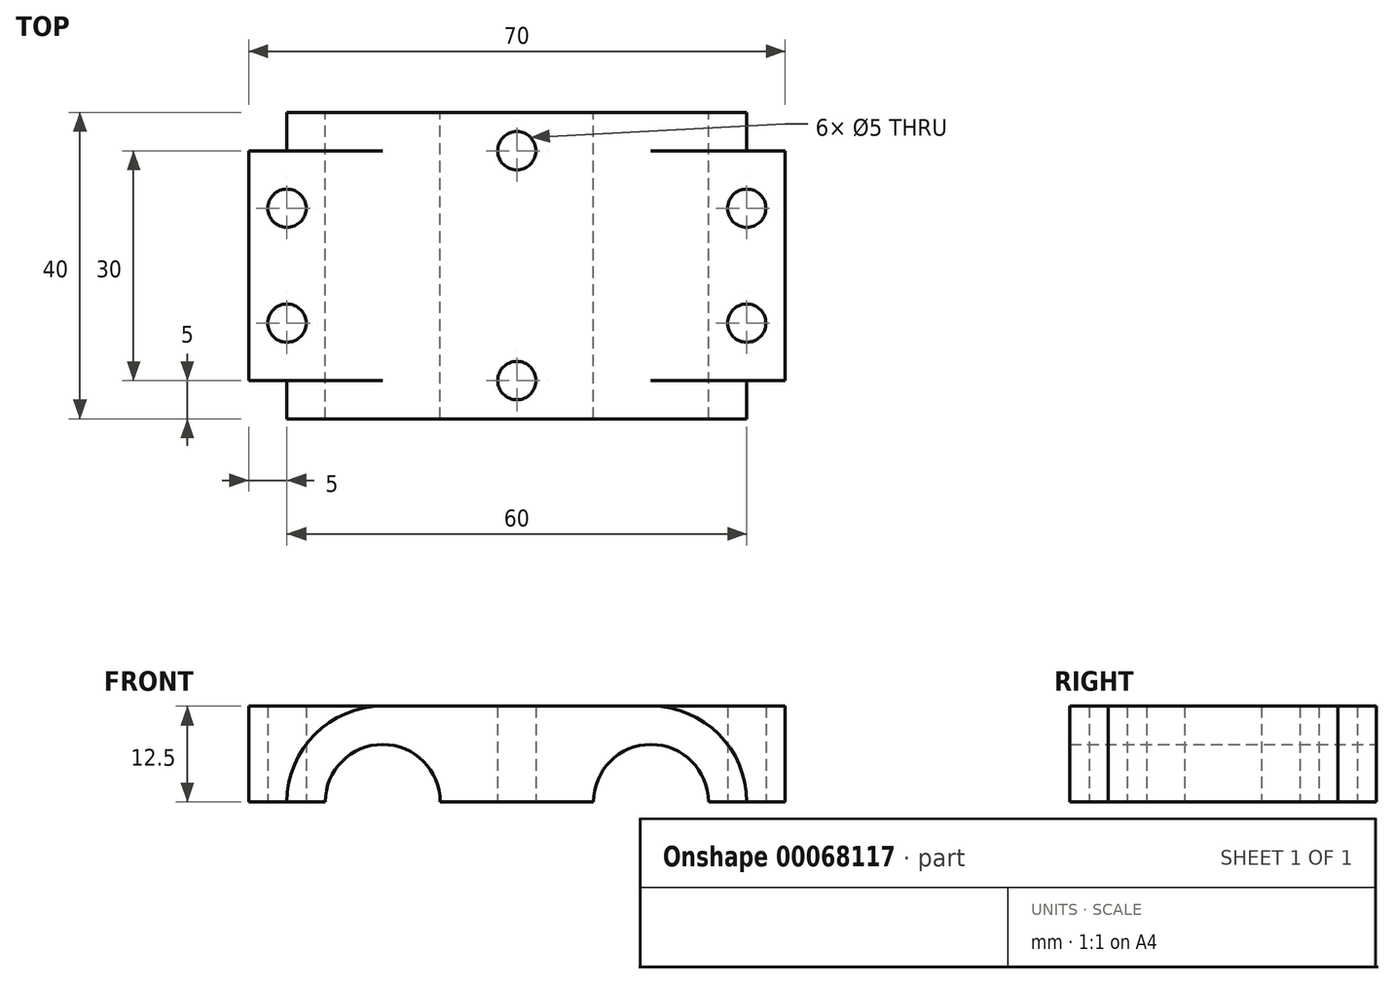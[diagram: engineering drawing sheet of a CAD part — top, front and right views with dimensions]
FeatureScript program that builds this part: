
annotation { "Feature Type Name" : "Feature", "Feature Type Description" : "" }
export const myFeature = defineFeature(function(context is Context, id is Id, definition is map)
    precondition{}
    {
        {
            var Q0;
            Q0=qCreatedBy(makeId("Front.planeOp"),FACE);
            var sketch = newSketch(context, id + "F0", { "sketchPlane" : qUnion([Q0])});
            skLineSegment(sketch, "E0.rect.bottom", {"start": v(-35, 6.25) * mm, "end": v(35, 6.25) * mm});
            skLineSegment(sketch, "E0.rect.top", {"start": v(-35, -6.25) * mm, "end": v(-25, -6.25) * mm});
            skLineSegment(sketch, "E0.rect.left", {"start": v(-35, 6.25) * mm, "end": v(-35, -6.25) * mm});
            skLineSegment(sketch, "E0.rect.right", {"start": v(35, 6.25) * mm, "end": v(35, -6.25) * mm});
            skPoint(sketch, "E0.rect.middle", {"position": v(0, 0) * mm});
            skArc(sketch, "E1", {"start": v(-10, -6.25) * mm, "mid": v(-17.5, 1.25) * mm, "end": v(-25, -6.25) * mm});
            skArc(sketch, "E2", {"start": v(25, -6.25) * mm, "mid": v(17.5, 1.25) * mm, "end": v(10, -6.25) * mm});
            skLineSegment(sketch, "E3.trimOffspring", {"start": v(-10, -6.25) * mm, "end": v(10, -6.25) * mm});
            skLineSegment(sketch, "E4.trimOffspring", {"start": v(25, -6.25) * mm, "end": v(35, -6.25) * mm});
            skSolve(sketch);
        }
        {
            var Q0;
            Q0=makeQuery(id+"F0.imprint","IMPRINT",FACE,{"disambiguationData":[TD([[makeQuery(id+"F0.imprint","IMPRINT",EDGE,{"derivedFrom":sQuery(id+"F0.wireOp",EDGE,"E0.rect.bottom")}),-1.0]])]});
            extrude(context, id + "F1", {"entities" : qUnion([Q0]), "endBound" : BoundingType.SYMMETRIC, "depth" : 30 * mm});
        }
        {
            var Q0;
            Q0=makeQuery(id+"F1.opExtrude","CAP_FACE",FACE,{"disambiguationData":[OSD([sQuery(id+"F0.wireOp",EDGE,"E0.rect.bottom"),sQuery(id+"F0.wireOp",EDGE,"E0.rect.top"),sQuery(id+"F0.wireOp",EDGE,"E0.rect.left"),sQuery(id+"F0.wireOp",EDGE,"E0.rect.right"),sQuery(id+"F0.wireOp",EDGE,"E1"),sQuery(id+"F0.wireOp",EDGE,"E2"),sQuery(id+"F0.wireOp",EDGE,"E3.trimOffspring"),sQuery(id+"F0.wireOp",EDGE,"E4.trimOffspring")])],"isStart":false});
            var sketch = newSketch(context, id + "F2", { "sketchPlane" : qUnion([Q0])});
            skLineSegment(sketch, "E5.0", {"start": v(-30, -6.25) * mm, "end": v(-25, -6.25) * mm});
            skArc(sketch, "E6.0", {"start": v(-10, -6.25) * mm, "mid": v(-17.5, 1.25) * mm, "end": v(-25, -6.25) * mm});
            skLineSegment(sketch, "E7.0", {"start": v(-10, -6.25) * mm, "end": v(10, -6.25) * mm});
            skArc(sketch, "E8.0", {"start": v(25, -6.25) * mm, "mid": v(17.5, 1.25) * mm, "end": v(10, -6.25) * mm});
            skLineSegment(sketch, "E9.0", {"start": v(25, -6.25) * mm, "end": v(30, -6.25) * mm});
            skLineSegment(sketch, "E10.0", {"start": v(-17.5, 6.25) * mm, "end": v(17.5, 6.25) * mm});
            skArc(sketch, "E11", {"start": v(-17.5, 6.25) * mm, "mid": v(-26.34, 2.59) * mm, "end": v(-30, -6.25) * mm});
            skArc(sketch, "E12", {"start": v(30, -6.25) * mm, "mid": v(26.34, 2.59) * mm, "end": v(17.5, 6.25) * mm});
            skPoint(sketch, "E13.orphan", {"position": v(-35, 6.25) * mm});
            skPoint(sketch, "E14.orphan", {"position": v(-35, -6.25) * mm});
            skPoint(sketch, "E15.orphan", {"position": v(35, 6.25) * mm});
            skPoint(sketch, "E16.orphan", {"position": v(35, -6.25) * mm});
            skSolve(sketch);
        }
        {
            var Q0;
            Q0=makeQuery(id+"F2.imprint","IMPRINT",FACE,{"disambiguationData":[TD([[makeQuery(id+"F2.imprint","IMPRINT",EDGE,{"derivedFrom":sQuery(id+"F2.wireOp",EDGE,"E5.0")}),1.0]])]});
            extrude(context, id + "F3", {"entities" : qUnion([Q0]), "operationType" : NewBodyOperationType.ADD, "depth" : 5 * mm});
        }
        {
            var Q0;
            Q0=makeQuery(id+"F1.opExtrude","SWEPT_BODY",BODY,{"disambiguationData":[OSD([sQuery(id+"F0.wireOp",EDGE,"E0.rect.bottom"),sQuery(id+"F0.wireOp",EDGE,"E0.rect.top"),sQuery(id+"F0.wireOp",EDGE,"E0.rect.left"),sQuery(id+"F0.wireOp",EDGE,"E0.rect.right"),sQuery(id+"F0.wireOp",EDGE,"E1"),sQuery(id+"F0.wireOp",EDGE,"E2"),sQuery(id+"F0.wireOp",EDGE,"E3.trimOffspring"),sQuery(id+"F0.wireOp",EDGE,"E4.trimOffspring")])]});
            var Q1;
            Q1=qCreatedBy(makeId("Front.planeOp"),FACE);
            mirror(context, id + "F4", {"operationType" : NewBodyOperationType.ADD, "entities" : qUnion([Q0]), "mirrorPlane" : qUnion([Q1])});
        }
        {
            var Q0;
            {var subQ0=makeQuery(id+"F3.boolean.opBoolean","MERGE",FACE,{"derivedFrom":[makeQuery(id+"F1.opExtrude","SWEPT_FACE",FACE,{"disambiguationData":[OSD([sQuery(id+"F0.wireOp",EDGE,"E3.trimOffspring")])]}),makeQuery(id+"F3.opExtrude","SWEPT_FACE",FACE,{"disambiguationData":[OSD([sQuery(id+"F2.wireOp",EDGE,"E7.0")])]})]});Q0=makeQuery(id+"F4.boolean.opBoolean","MERGE",FACE,{"derivedFrom":[subQ0,makeQuery(id+"F4.opPattern","COPY",FACE,{"derivedFrom":subQ0,"instanceName":"1"})]});}
            var sketch = newSketch(context, id + "F5", { "sketchPlane" : qUnion([Q0])});
            skPoint(sketch, "E17", {"position": v(-30, 7.5) * mm});
            skPoint(sketch, "E18", {"position": v(-30, -7.5) * mm});
            skPoint(sketch, "E19", {"position": v(0, -15) * mm});
            skPoint(sketch, "E20", {"position": v(0, 15) * mm});
            skPoint(sketch, "E21", {"position": v(30, 7.5) * mm});
            skPoint(sketch, "E22", {"position": v(30, -7.5) * mm});
            skSolve(sketch);
        }
        {
            var Q0;
            Q0=sQuery(id+"F5.wireOp",VERTEX,"E17");
            var Q1;
            Q1=sQuery(id+"F5.wireOp",VERTEX,"E18");
            var Q2;
            Q2=sQuery(id+"F5.wireOp",VERTEX,"E20");
            var Q3;
            Q3=sQuery(id+"F5.wireOp",VERTEX,"E19");
            var Q4;
            Q4=sQuery(id+"F5.wireOp",VERTEX,"E21");
            var Q5;
            Q5=sQuery(id+"F5.wireOp",VERTEX,"E22");
            var Q6;
            Q6=makeQuery(id+"F1.opExtrude","SWEPT_BODY",BODY,{"disambiguationData":[OSD([sQuery(id+"F0.wireOp",EDGE,"E0.rect.bottom"),sQuery(id+"F0.wireOp",EDGE,"E0.rect.top"),sQuery(id+"F0.wireOp",EDGE,"E0.rect.left"),sQuery(id+"F0.wireOp",EDGE,"E0.rect.right"),sQuery(id+"F0.wireOp",EDGE,"E1"),sQuery(id+"F0.wireOp",EDGE,"E2"),sQuery(id+"F0.wireOp",EDGE,"E3.trimOffspring"),sQuery(id+"F0.wireOp",EDGE,"E4.trimOffspring")])]});
            hole(context, id + "F6", {"style" : HoleStyle.SIMPLE, "holeDiameter" : 5 * mm, "endStyle" : HoleEndStyle.THROUGH, "locations" : qUnion([Q0, Q1, Q2, Q3, Q4, Q5]), "scope" : qUnion([Q6])});
        }
    });
